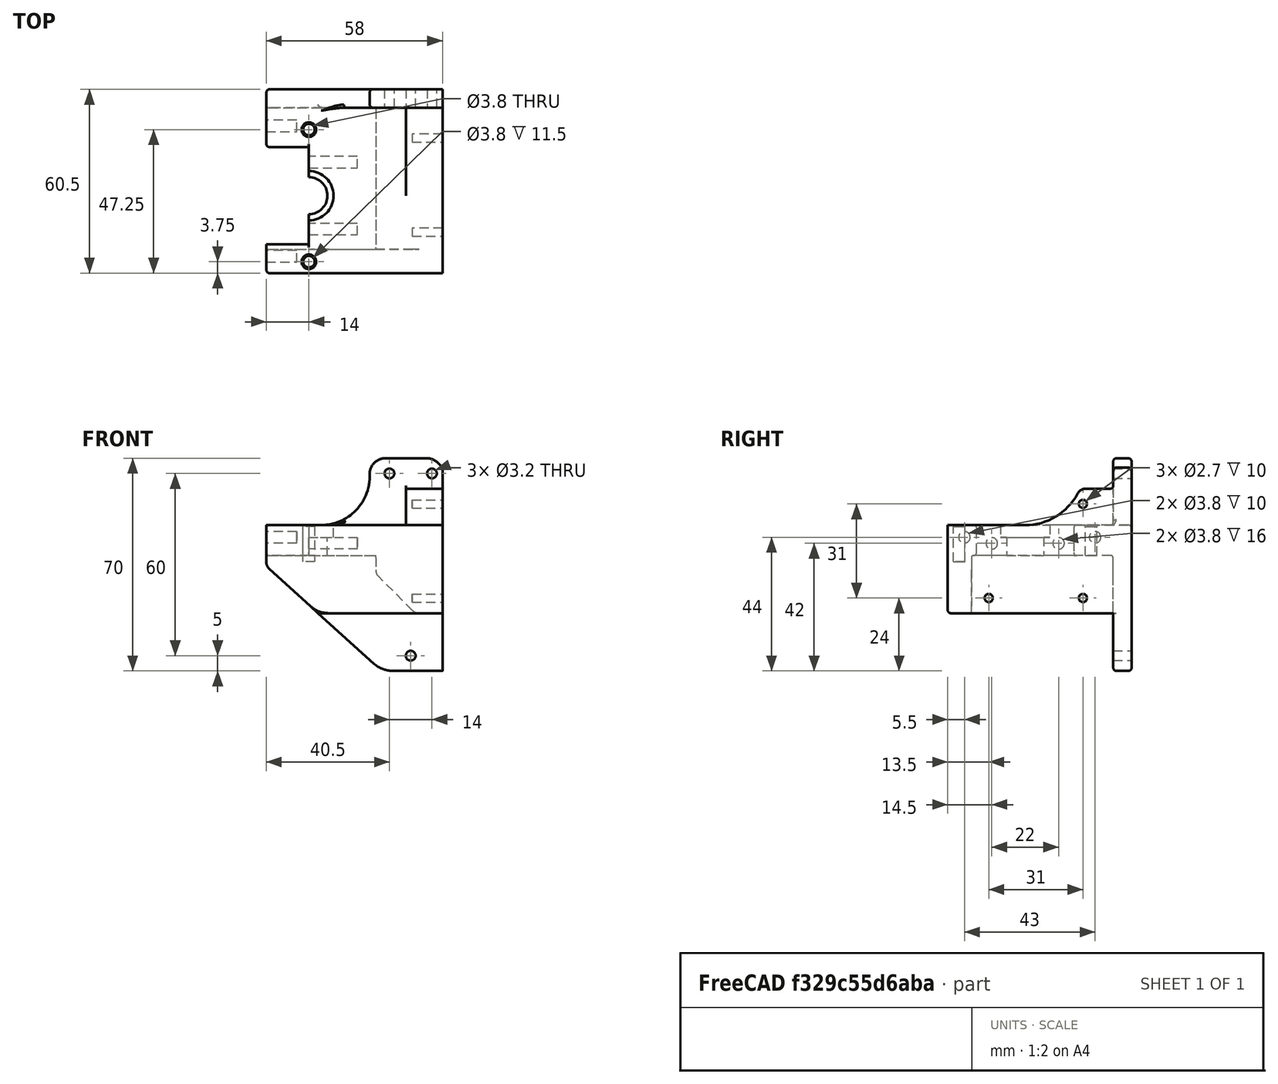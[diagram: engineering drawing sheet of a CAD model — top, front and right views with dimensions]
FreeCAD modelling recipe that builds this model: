
FCSTD DOCUMENT  (FreeCAD 0.19R)
Label: head9.2
License: All rights reserved
LicenseURL: http://en.wikipedia.org/wiki/All_rights_reserved
objects: PartDesign::Fillet×16, Sketcher::SketchObject×14, PartDesign::Pocket×13, PartDesign::Chamfer×3, PartDesign::Pad×1, PartDesign::Body×1, Mesh::Feature×1
note: 81 computed .brp shape members not serialized (recipe doc carries the construction recipe); baked Part::Feature solids carry a one-line shape summary decoded from their .brp

FEATURE [Sketcher::SketchObject] Sketch
  FullyConstrained = true
  MapMode = 5
  Support = -> [XY_Plane]
  sketch-geometry (5):
    g0: LineSegment StartX=0 StartY=0 StartZ=0 EndX=44 EndY=0 EndZ=0
    g1: LineSegment StartX=-14 StartY=0 StartZ=0 EndX=0 EndY=0 EndZ=0
    g2: LineSegment StartX=-14 StartY=0 StartZ=0 EndX=-14 EndY=-60.5 EndZ=0
    g3: LineSegment StartX=-14 StartY=-60.5 StartZ=0 EndX=44 EndY=-60.5 EndZ=0
    g4: LineSegment StartX=44 StartY=-60.5 StartZ=0 EndX=44 EndY=0 EndZ=0
  constraints (14):
    c: Coincident(g-1,g0)
    c: PointOnObject(g0,g-1)
    c: PointOnObject(g1,g-1)
    c: Coincident(g1,g0)
    c: Coincident(g1,g2)
    c: Vertical(g2)
    c: Coincident(g2,g3)
    c: Horizontal(g3)
    c: Coincident(g3,g4)
    c: Coincident(g4,g0)
    c: Vertical(g4)
    c: Distance(g4) = 60.5
    c: DistanceX(g0) = 44
    c: DistanceX(g1) = -14
FEATURE [PartDesign::Pad] Pad
  Direction = (1,1,1)
  Length = 70
  Length2 = 100
  Profile = -> Sketch
  Type = 0
FEATURE [Sketcher::SketchObject] Sketch002  label="platformnotch"
  FullyConstrained = false
  MapMode = 5
  Placement = pos=(0,0,70) rot=(0,0,1;0rad)
  Support = -> [Pad]
  sketch-geometry (6):
    g0: LineSegment StartX=32 StartY=-6 StartZ=0 EndX=32 EndY=-65.096 EndZ=0
    g1: LineSegment StartX=32 StartY=-65.096 StartZ=0 EndX=-40.7834 EndY=-65.096 EndZ=0
    g2: LineSegment StartX=-40.7834 StartY=-65.096 StartZ=0 EndX=-40.7834 EndY=12.9948 EndZ=0
    g3: LineSegment StartX=-40.7834 StartY=12.9948 StartZ=0 EndX=20 EndY=12.9948 EndZ=0
    g4: LineSegment StartX=20 StartY=12.9948 StartZ=0 EndX=20 EndY=-6 EndZ=0
    g5: LineSegment StartX=20 StartY=-6 StartZ=0 EndX=32 EndY=-6 EndZ=0
  constraints (15):
    c: Coincident(g0,g1)
    c: Coincident(g1,g2)
    c: Horizontal(g1)
    c: Vertical(g0)
    c: Vertical(g2)
    c: DistanceX(g0) = 32
    c: DistanceY(g0) = -6
    c: Coincident(g2,g3)
    c: Horizontal(g3)
    c: Coincident(g3,g4)
    c: Coincident(g4,g5)
    c: Coincident(g5,g0)
    c: Horizontal(g5)
    c: Vertical(g4)
    c: DistanceX(g3) = 20
FEATURE [PartDesign::Pocket] Pocket
  BaseFeature = -> Pad
  Length = 22
  Length2 = 100
  Profile = -> Sketch002
  Type = 0
FEATURE [Sketcher::SketchObject] Sketch008  label="pcbnotches"
  FullyConstrained = false
  MapMode = 5
  Placement = pos=(44,0,0) rot=(0.57735,0.57735,0.57735;2.0944rad)
  Support = -> [Pocket]
  sketch-geometry (8):
    g0: LineSegment StartX=-67.659 StartY=19 StartZ=0 EndX=-6 EndY=19 EndZ=0
    g1: LineSegment StartX=-6 StartY=19 StartZ=0 EndX=-6 EndY=-22.4626 EndZ=0
    g2: LineSegment StartX=-6 StartY=-22.4626 StartZ=0 EndX=-67.659 EndY=-22.4626 EndZ=0
    g3: LineSegment StartX=-67.659 StartY=-22.4626 StartZ=0 EndX=-67.659 EndY=19 EndZ=0
    g4: LineSegment StartX=-66.332 StartY=73.6841 StartZ=0 EndX=-6 EndY=73.6841 EndZ=0
    g5: LineSegment StartX=-6 StartY=73.6841 StartZ=0 EndX=-6 EndY=60 EndZ=0
    g6: LineSegment StartX=-6 StartY=60 StartZ=0 EndX=-66.332 EndY=60 EndZ=0
    g7: LineSegment StartX=-66.332 StartY=60 StartZ=0 EndX=-66.332 EndY=73.6841 EndZ=0
  constraints (20):
    c: Coincident(g0,g1)
    c: Coincident(g1,g2)
    c: Coincident(g2,g3)
    c: Coincident(g3,g0)
    c: Horizontal(g0)
    c: Horizontal(g2)
    c: Vertical(g1)
    c: Vertical(g3)
    c: DistanceY(g0) = 19
    c: Coincident(g4,g5)
    c: Coincident(g5,g6)
    c: Coincident(g6,g7)
    c: Coincident(g7,g4)
    c: Horizontal(g4)
    c: Horizontal(g6)
    c: Vertical(g5)
    c: Vertical(g7)
    c: DistanceX(g4) = -6
    c: DistanceY(g5) = 60
    c: DistanceX(g0) = -6
FEATURE [PartDesign::Pocket] Pocket001
  BaseFeature = -> Pocket
  Length = 76
  Length2 = 100
  Profile = -> Sketch008
  Type = 0
FEATURE [Sketcher::SketchObject] Sketch003  label="extredureholes"
  FullyConstrained = true
  MapMode = 5
  Placement = pos=(0,0,48) rot=(0,0,1;0rad)
  Support = -> [Pocket001]
  sketch-geometry (3):
    g0: Circle CenterX=0 CenterY=-13.25 CenterZ=0 NormalX=0 NormalY=0 NormalZ=1 AngleXU=0 Radius=1.9
    g1: Circle CenterX=0 CenterY=-56.75 CenterZ=0 NormalX=0 NormalY=0 NormalZ=1 AngleXU=0 Radius=1.9
    g2: LineSegment StartX=-14.87 StartY=-35 StartZ=0 EndX=14.87 EndY=-35 EndZ=0
  constraints (8):
    c: Distance(g1,g0) = 43.5
    c: Diameter(g1) = 3.8
    c: PointOnObject(g0,g-2)
    c: Symmetric(g2,g2,g-2)
    c: Distance(g2) = 29.74
    c: Symmetric(g1,g0,g2)
    c: DistanceY(g2) = -35
    c: Diameter(g0) = 3.8
FEATURE [PartDesign::Pocket] Pocket002
  BaseFeature = -> Pocket001
  Length = 12
  Length2 = 100
  Profile = -> Sketch003
  Type = 0
FEATURE [Sketcher::SketchObject] Sketch004  label="topNotch"
  FullyConstrained = true
  MapMode = 5
  Placement = pos=(0,0,48) rot=(0,0,1;0rad)
  Support = -> [Pocket002]
  sketch-geometry (4):
    g0: ArcOfCircle CenterX=0 CenterY=-35 CenterZ=0 NormalX=0 NormalY=0 NormalZ=1 AngleXU=0 Radius=8.125 StartAngle=4.71239 EndAngle=7.85398
    g1: LineSegment StartX=-1.5e-15 StartY=-43.125 StartZ=0 EndX=-25 EndY=-43.125 EndZ=0
    g2: LineSegment StartX=-25 StartY=-43.125 StartZ=0 EndX=-25 EndY=-26.875 EndZ=0
    g3: LineSegment StartX=-25 StartY=-26.875 StartZ=0 EndX=-2.629e-13 EndY=-26.875 EndZ=0
  constraints (11):
    c: PointOnObject(g0,g-2)
    c: Diameter(g0) = 16.25
    c: DistanceY(g0) = -35
    c: Coincident(g1,g2)
    c: Coincident(g2,g3)
    c: Distance(g3) = 25
    c: Tangent(g3,g0) = 1.5708
    c: Tangent(g1,g0) = 1.5708
    c: Horizontal(g3)
    c: Horizontal(g1)
    c: Vertical(g2)
FEATURE [PartDesign::Pocket] Pocket003
  BaseFeature = -> Pocket002
  Length = 4
  Length2 = 100
  Profile = -> Sketch004
  Type = 0
FEATURE [Sketcher::SketchObject] Sketch018  label="innergroove"
  FullyConstrained = true
  MapMode = 5
  Placement = pos=(0,0,44) rot=(0,0,1;0rad)
  Support = -> [Pocket003]
  sketch-geometry (4):
    g0: ArcOfCircle CenterX=0 CenterY=-35 CenterZ=0 NormalX=0 NormalY=0 NormalZ=1 AngleXU=0 Radius=6.1 StartAngle=4.71239 EndAngle=7.85398
    g1: LineSegment StartX=-1.1e-15 StartY=-41.1 StartZ=0 EndX=-50 EndY=-41.1 EndZ=0
    g2: LineSegment StartX=1.9e-15 StartY=-28.9 StartZ=0 EndX=-50 EndY=-28.9 EndZ=0
    g3: LineSegment StartX=-50 StartY=-41.1 StartZ=0 EndX=-50 EndY=-28.9 EndZ=0
  constraints (11):
    c: PointOnObject(g0,g-2)
    c: Coincident(g3,g1)
    c: Coincident(g3,g2)
    c: Tangent(g1,g0) = 1.5708
    c: Tangent(g2,g0) = -1.5708
    c: DistanceY(g0) = -35
    c: Diameter(g0) = 12.2
    c: Distance(g1) = 50
    c: Vertical(g3)
    c: Horizontal(g1)
    c: Horizontal(g2)
FEATURE [PartDesign::Pocket] Pocket004
  BaseFeature = -> Pocket003
  Length = 6
  Length2 = 100
  Profile = -> Sketch018
  Type = 0
FEATURE [Sketcher::SketchObject] Sketch009  label="PCBholes"
  FullyConstrained = true
  MapMode = 5
  Placement = pos=(44,0,0) rot=(0.57735,0.57735,0.57735;2.0944rad)
  Support = -> [Pocket004]
  sketch-geometry (5):
    g0: Circle CenterX=-47 CenterY=55 CenterZ=0 NormalX=0 NormalY=0 NormalZ=1 AngleXU=0 Radius=1.35
    g1: Circle CenterX=-16 CenterY=24 CenterZ=0 NormalX=0 NormalY=0 NormalZ=1 AngleXU=0 Radius=1.35
    g2: LineSegment StartX=-47 StartY=55 StartZ=0 EndX=-16 EndY=24 EndZ=0
    g3: Circle CenterX=-16 CenterY=55 CenterZ=0 NormalX=0 NormalY=0 NormalZ=1 AngleXU=0 Radius=1.35
    g4: Circle CenterX=-47 CenterY=24 CenterZ=0 NormalX=0 NormalY=0 NormalZ=1 AngleXU=0 Radius=1.35
  constraints (14):
    c: Coincident(g2,g0)
    c: Coincident(g2,g1)
    c: Angle(g2) = -0.785398
    c: DistanceX(g1) = -16
    c: DistanceY(g1) = 24
    c: Diameter(g4) = 2.7
    c: Equal(g4,g0)
    c: Equal(g4,g3)
    c: Equal(g4,g1)
    c: DistanceY(g4,g0) = 31
    c: DistanceX(g0,g3) = 31
    c: DistanceX(g4,g1) = 31
    c: DistanceY(g4) = 24
    c: DistanceY(g1,g3) = 31
FEATURE [PartDesign::Pocket] Pocket005
  BaseFeature = -> Pocket004
  Length = 10
  Length2 = 100
  Profile = -> Sketch009
  Type = 0
FEATURE [Sketcher::SketchObject] Sketch030
  FullyConstrained = false
  MapMode = 5
  Placement = pos=(0,0,48) rot=(0,0,1;0rad)
  Support = -> [Pocket005]
  sketch-geometry (5):
    g0: LineSegment StartX=-28.769 StartY=-19 StartZ=0 EndX=0 EndY=-19 EndZ=0
    g1: LineSegment StartX=0 StartY=-19 StartZ=0 EndX=0 EndY=-51 EndZ=0
    g2: LineSegment StartX=0 StartY=-51 StartZ=0 EndX=-28.769 EndY=-51 EndZ=0
    g3: LineSegment StartX=-28.769 StartY=-51 StartZ=0 EndX=-28.769 EndY=-19 EndZ=0
    g4: LineSegment StartX=-7.77915 StartY=-35 StartZ=0 EndX=15.2351 EndY=-35 EndZ=0
  constraints (12):
    c: Coincident(g0,g1)
    c: Coincident(g1,g2)
    c: Coincident(g2,g3)
    c: Coincident(g3,g0)
    c: Horizontal(g0)
    c: Horizontal(g2)
    c: Vertical(g1)
    c: Vertical(g3)
    c: PointOnObject(g1,g-2)
    c: Distance(g1) = 32
    c: Symmetric(g0,g1,g4)
    c: DistanceY(g4) = -35
FEATURE [PartDesign::Pocket] Pocket006
  BaseFeature = -> Pocket005
  Length = 5
  Length2 = 100
  Profile = -> Sketch030
  Type = 1
FEATURE [Sketcher::SketchObject] Sketch031
  FullyConstrained = false
  MapMode = 5
  Placement = pos=(-14,0,0) rot=(0.57735,-0.57735,-0.57735;2.0944rad)
  Support = -> [Pocket006]
  sketch-geometry (4):
    g0: LineSegment StartX=6.1 StartY=38 StartZ=0 EndX=52.7193 EndY=38 EndZ=0
    g1: LineSegment StartX=52.7193 StartY=38 StartZ=0 EndX=52.7193 EndY=2.95128 EndZ=0
    g2: LineSegment StartX=52.7193 StartY=2.95128 StartZ=0 EndX=6.1 EndY=2.95128 EndZ=0
    g3: LineSegment StartX=6.1 StartY=2.95128 StartZ=0 EndX=6.1 EndY=38 EndZ=0
  constraints (10):
    c: Coincident(g0,g1)
    c: Coincident(g1,g2)
    c: Coincident(g2,g3)
    c: Coincident(g3,g0)
    c: Horizontal(g0)
    c: Horizontal(g2)
    c: Vertical(g1)
    c: Vertical(g3)
    c: DistanceX(g0) = 6.1
    c: DistanceY(g0) = 38
FEATURE [PartDesign::Pocket] Pocket007
  BaseFeature = -> Pocket006
  Length = 36
  Length2 = 100
  Profile = -> Sketch031
  Type = 0
FEATURE [Sketcher::SketchObject] Sketch032  label="FanScrews"
  ExternalGeometry = -> [Pocket007]
  FullyConstrained = true
  MapMode = 5
  Placement = pos=(-14,0,0) rot=(0.57735,-0.57735,-0.57735;2.0944rad)
  Support = -> [Pocket007]
  sketch-geometry (2):
    g0: Circle CenterX=12 CenterY=44 CenterZ=0 NormalX=0 NormalY=0 NormalZ=1 AngleXU=0 Radius=1.9
    g1: Circle CenterX=55 CenterY=44 CenterZ=0 NormalX=0 NormalY=0 NormalZ=1 AngleXU=0 Radius=1.9
  constraints (6):
    c: Diameter(g0) = 3.8
    c: DistanceX(g0) = 12
    c: DistanceY(g0) = 44
    c: Diameter(g1) = 3.8
    c: DistanceY(g1) = 44
    c: DistanceX(g1) = 55
FEATURE [PartDesign::Pocket] Pocket008
  BaseFeature = -> Pocket007
  Length = 10
  Length2 = 100
  Profile = -> Sketch032
  Type = 0
FEATURE [Sketcher::SketchObject] Sketch013  label="groovescrews"
  FullyConstrained = false
  MapMode = 5
  Placement = pos=(0,0,0) rot=(0.57735,-0.57735,-0.57735;2.0944rad)
  Support = -> [Pocket008]
  sketch-geometry (3):
    g0: Circle CenterX=24 CenterY=42 CenterZ=0 NormalX=0 NormalY=0 NormalZ=1 AngleXU=0 Radius=1.9
    g1: Circle CenterX=46 CenterY=42 CenterZ=0 NormalX=0 NormalY=0 NormalZ=1 AngleXU=0 Radius=1.9
    g2: LineSegment StartX=35 StartY=87.2769 StartZ=0 EndX=35 EndY=69.6255 EndZ=0
  constraints (6):
    c: Distance(g1,g0) = 22
    c: Diameter(g1) = 3.8
    c: Equal(g1,g0)
    c: Vertical(g2)
    c: Symmetric(g1,g0,g2)
    c: DistanceX(g2) = 35
FEATURE [PartDesign::Pocket] Pocket009
  BaseFeature = -> Pocket008
  Length = 16
  Length2 = 100
  Profile = -> Sketch013
  Type = 0
FEATURE [Sketcher::SketchObject] Sketch010  label="mountholes"
  FullyConstrained = true
  MapMode = 5
  Placement = pos=(0,0,0) rot=(0,0.707107,0.707107;3.14159rad)
  Support = -> [Pocket009]
  sketch-geometry (3):
    g0: Circle CenterX=-33.5 CenterY=5 CenterZ=0 NormalX=0 NormalY=0 NormalZ=1 AngleXU=0 Radius=1.6
    g1: Circle CenterX=-40.5 CenterY=65 CenterZ=0 NormalX=0 NormalY=0 NormalZ=1 AngleXU=0 Radius=1.6
    g2: Circle CenterX=-26.5 CenterY=65 CenterZ=0 NormalX=0 NormalY=0 NormalZ=1 AngleXU=0 Radius=1.6
  constraints (9):
    c: Diameter(g0) = 3.2
    c: Equal(g0,g2)
    c: Equal(g0,g1)
    c: DistanceX(g0) = -33.5
    c: Distance(g1,g2) = 14
    c: DistanceX(g2) = -26.5
    c: DistanceY(g0) = 5
    c: DistanceY(g2) = 65
    c: DistanceY(g1) = 65
FEATURE [PartDesign::Pocket] Pocket010
  BaseFeature = -> Pocket009
  Length = 7
  Length2 = 100
  Profile = -> Sketch010
  Type = 0
FEATURE [Sketcher::SketchObject] Sketch033  label="ANgler"
  FullyConstrained = false
  MapMode = 5
  Placement = pos=(0,0,0) rot=(0,0.707107,0.707107;3.14159rad)
  Support = -> [Pocket010]
  sketch-geometry (3):
    g0: LineSegment StartX=21.9958 StartY=41.6537 StartZ=0 EndX=-34.9081 EndY=-9.83073 EndZ=0
    g1: LineSegment StartX=21.9958 StartY=41.6537 StartZ=0 EndX=21.9958 EndY=-12.4114 EndZ=0
    g2: LineSegment StartX=21.9958 StartY=-12.4114 StartZ=0 EndX=-34.9081 EndY=-9.83073 EndZ=0
  constraints (4):
    c: Coincident(g0,g1)
    c: Vertical(g1)
    c: Coincident(g1,g2)
    c: Coincident(g2,g0)
FEATURE [PartDesign::Pocket] Pocket011
  BaseFeature = -> Pocket010
  Length = 5
  Length2 = 100
  Profile = -> Sketch033
  Type = 1
FEATURE [Sketcher::SketchObject] Sketch034
  ExternalGeometry = -> [Pocket011]
  FullyConstrained = true
  MapMode = 5
  Placement = pos=(32,0,0) rot=(0.57735,-0.57735,-0.57735;2.0944rad)
  Support = -> [Pocket011]
  sketch-geometry (4):
    g0: ArcOfCircle CenterX=35 CenterY=67.5 CenterZ=0 NormalX=0 NormalY=0 NormalZ=1 AngleXU=0 Radius=19.5 StartAngle=3.14159 EndAngle=4.71239
    g1: LineSegment StartX=35 StartY=48 StartZ=0 EndX=74.47 EndY=48 EndZ=0
    g2: LineSegment StartX=15.5 StartY=67.5 StartZ=0 EndX=74.47 EndY=67.5 EndZ=0
    g3: LineSegment StartX=74.47 StartY=67.5 StartZ=0 EndX=74.47 EndY=48 EndZ=0
  constraints (13):
    c: DistanceX(g0) = 35
    c: Diameter(g0) = 39
    c: Coincident(g1,g0)
    c: Horizontal(g1)
    c: Coincident(g0,g2)
    c: Coincident(g2,g3)
    c: Coincident(g3,g1)
    c: Horizontal(g2)
    c: Perpendicular(g0,g2)
    c: PointOnObject(g-3,g1)
    c: Vertical(g3)
    c: Distance(g2) = 58.97
    c: DistanceX(g0) = 35
FEATURE [PartDesign::Pocket] Pocket012
  BaseFeature = -> Pocket011
  Length = 10
  Length2 = 100
  Profile = -> Sketch034
  Type = 1
FEATURE [PartDesign::Fillet] Fillet
  Base = -> Pocket012 [Edge65]
  BaseFeature = -> Pocket012
  Radius = 3
  SupportTransform = false
FEATURE [PartDesign::Chamfer] Chamfer
  Angle = 45
  Base = -> Fillet [Edge5,Edge25]
  BaseFeature = -> Fillet
  ChamferType = 0
  FlipDirection = false
  Size = 3
  Size2 = 1
  SupportTransform = false
FEATURE [PartDesign::Fillet] Fillet001
  Base = -> Chamfer [Edge20,Edge61,Edge72]
  BaseFeature = -> Chamfer
  Radius = 5
  SupportTransform = false
FEATURE [PartDesign::Fillet] Fillet002
  Base = -> Fillet001 [Edge50,Edge63]
  BaseFeature = -> Fillet001
  Radius = 9
  SupportTransform = false
FEATURE [PartDesign::Fillet] Fillet003
  Base = -> Fillet002 [Edge104,Edge134]
  BaseFeature = -> Fillet002
  Radius = 0.7
  SupportTransform = false
FEATURE [PartDesign::Fillet] Fillet004
  Base = -> Fillet003 [Edge20,Edge27]
  BaseFeature = -> Fillet003
  Radius = 1
  SupportTransform = false
FEATURE [PartDesign::Fillet] Fillet005
  Base = -> Fillet004 [Edge36,Edge27]
  BaseFeature = -> Fillet004
  Radius = 1
  SupportTransform = false
FEATURE [PartDesign::Fillet] Fillet006
  Base = -> Fillet005 [Edge104,Edge8]
  BaseFeature = -> Fillet005
  Radius = 3
  SupportTransform = false
FEATURE [PartDesign::Fillet] Fillet007
  Base = -> Fillet006 [Edge61]
  BaseFeature = -> Fillet006
  Radius = 1
  SupportTransform = false
FEATURE [PartDesign::Fillet] Fillet008
  Base = -> Fillet007 [Edge72]
  BaseFeature = -> Fillet007
  Radius = 1
  SupportTransform = false
FEATURE [PartDesign::Chamfer] Chamfer001
  Angle = 45
  Base = -> Fillet008 [Edge185]
  BaseFeature = -> Fillet008
  ChamferType = 0
  FlipDirection = false
  Size = 13
  Size2 = 1
  SupportTransform = false
FEATURE [PartDesign::Fillet] Fillet009
  Base = -> Chamfer001 [Edge59]
  BaseFeature = -> Chamfer001
  Radius = 1
  SupportTransform = false
FEATURE [PartDesign::Fillet] Fillet010
  Base = -> Fillet009 [Edge143]
  BaseFeature = -> Fillet009
  Radius = 16
  SupportTransform = false
FEATURE [PartDesign::Fillet] Fillet011
  Base = -> Fillet010 [Edge151]
  BaseFeature = -> Fillet010
  Radius = 1
  SupportTransform = false
FEATURE [PartDesign::Fillet] Fillet012
  Base = -> Fillet011 [Edge78]
  BaseFeature = -> Fillet011
  Radius = 1
  SupportTransform = false
FEATURE [PartDesign::Fillet] Fillet013
  Base = -> Fillet012 [Edge91]
  BaseFeature = -> Fillet012
  Radius = 1
  SupportTransform = false
FEATURE [PartDesign::Fillet] Fillet014
  Base = -> Fillet013 [Edge24]
  BaseFeature = -> Fillet013
  Radius = 1
  SupportTransform = false
FEATURE [PartDesign::Fillet] Fillet015
  Base = -> Fillet014 [Edge189,Edge95]
  BaseFeature = -> Fillet014
  Radius = 3
  SupportTransform = false
FEATURE [PartDesign::Chamfer] Chamfer002
  Angle = 45
  Base = -> Fillet015 [Edge192,Vertex138,Edge191]
  BaseFeature = -> Fillet015
  ChamferType = 0
  FlipDirection = false
  Size = 0.5
  Size2 = 1
  SupportTransform = false
FEATURE [PartDesign::Body] Body
  Group = -> [Sketch,Pad,Sketch002,Sketch003,Sketch004,Sketch008,Sketch009,Sketch010,Sketch013,Sketch018,Pocket,Pocket001,Pocket002,Pocket003,Pocket004,Pocket005,Sketch030,Pocket006,Sketch031,Pocket007,Sketch032,Pocket008,Pocket009,Pocket010,Sketch033,Pocket011,Sketch034,Pocket012,Fillet,Chamfer,Fillet001,Fillet002,Fillet003,Fillet004,Fillet005,Fillet006,Fillet007,Fillet008,Chamfer001,Fillet009,Fillet010,+6 more]
  Origin = -> Origin
  Tip = -> Chamfer002
FEATURE [Mesh::Feature] Mesh  label="Chamfer002 (Meshed)"
